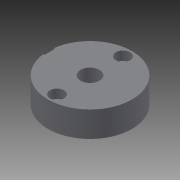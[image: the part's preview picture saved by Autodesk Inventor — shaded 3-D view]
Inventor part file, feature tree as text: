
AUTODESK INVENTOR PART (.ipt)
format: ipt  version: 2014 (Build 180170000, 170)  size: 225,792 bytes
history: native  units: in
note: dims shown in document units (in); Inventor stores cm internally (conversion verified against a paired STEP export)
features: other x189, sketch x10, hole x7, revolve x3, thread x1
ambient origin geometry x8: Origin, YZ Plane, XZ Plane, XY Plane, X Axis, Y Axis, Z Axis, Center Point
bodies: Solid1 (feature_tree)
feature tree (210):
  revolve  "Revolution1"  Angle=360.0deg
  revolve  "Revolution2"  Angle=360.0deg
  thread  "Thread1"  [1 undecoded]
  hole  "Hole1"  [1 undecoded]
  revolve  "Revolution3"  [1 undecoded]
  hole  "Hole2"  [1 undecoded]
  hole  "Hole3"  [1 undecoded]
  hole  "Hole4"  [1 undecoded]
  hole  "Hole5"  [1 undecoded]
  hole  "Hole6"  [1 undecoded]
  hole  "Hole7"  [1 undecoded]
  other  "a1_XY"
  other  "a1_YZ"
  other  "a1_ZX"
  other  "a1_X"
  other  "a1_Y"
  other  "a1_Z"
  other  "a1_Center"
  other  "a2_XY"
  other  "a2_YZ"
  other  "a2_ZX"
  other  "a2_X"
  other  "a2_Y"
  other  "a2_Z"
  other  "a2_Center"
  other  "ar3_XY"
  other  "ar3_YZ"
  other  "ar3_ZX"
  other  "ar3_X"
  other  "ar3_Y"
  other  "ar3_Z"
  other  "ar3_Center"
  other  "ar4_XY"
  other  "ar4_YZ"
  other  "ar4_ZX"
  other  "ar4_X"
  other  "ar4_Y"
  other  "ar4_Z"
  other  "ar4_Center"
  other  "ar5_XY"
  other  "ar5_YZ"
  other  "ar5_ZX"
  other  "ar5_X"
  other  "ar5_Y"
  other  "ar5_Z"
  other  "ar5_Center"
  other  "ar6_XY"
  other  "ar6_YZ"
  other  "ar6_ZX"
  other  "ar6_X"
  other  "ar6_Y"
  other  "ar6_Z"
  other  "ar6_Center"
  other  "b1_XY"
  other  "b1_YZ"
  other  "b1_ZX"
  other  "b1_X"
  other  "b1_Y"
  other  "b1_Z"
  other  "b1_Center"
  other  "c1_XY"
  other  "c1_YZ"
  other  "c1_ZX"
  other  "c1_X"
  other  "c1_Y"
  other  "c1_Z"
  other  "c1_Center"
  other  "c2_XY"
  other  "c2_YZ"
  other  "c2_ZX"
  other  "c2_X"
  other  "c2_Y"
  other  "c2_Z"
  other  "c2_Center"
  other  "d1_XY"
  other  "d1_YZ"
  other  "d1_ZX"
  other  "d1_X"
  other  "d1_Y"
  other  "d1_Z"
  other  "d1_Center"
  other  "d2_XY"
  other  "d2_YZ"
  other  "d2_ZX"
  other  "d2_X"
  other  "d2_Y"
  other  "d2_Z"
  other  "d2_Center"
  other  "j_XY"
  other  "j_YZ"
  other  "j_ZX"
  other  "j_X"
  other  "j_Y"
  other  "j_Z"
  other  "j_Center"
  other  "k1_XY"
  other  "k1_YZ"
  other  "k1_ZX"
  other  "k1_X"
  other  "k1_Y"
  other  "k1_Z"
  other  "k1_Center"
  other  "k2_XY"
  other  "k2_YZ"
  other  "k2_ZX"
  other  "k2_X"
  other  "k2_Y"
  other  "k2_Z"
  other  "k2_Center"
  other  "l1_XY"
  other  "l1_YZ"
  other  "l1_ZX"
  other  "l1_X"
  other  "l1_Y"
  other  "l1_Z"
  other  "l1_Center"
  other  "l2_XY"
  other  "l2_YZ"
  other  "l2_ZX"
  other  "l2_X"
  other  "l2_Y"
  other  "l2_Z"
  other  "l2_Center"
  other  "rg_XY"
  other  "rg_YZ"
  other  "rg_ZX"
  other  "rg_X"
  other  "rg_Y"
  other  "rg_Z"
  other  "rg_Center"
  other  "rh_XY"
  other  "rh_YZ"
  other  "rh_ZX"
  other  "rh_X"
  other  "rh_Y"
  other  "rh_Z"
  other  "rh_Center"
  other  "to_dummy_XY"
  other  "to_dummy_YZ"
  other  "to_dummy_ZX"
  other  "to_dummy_X"
  other  "to_dummy_Y"
  other  "to_dummy_Z"
  other  "to_dummy_Center"
  other  "to_nut_XY"
  other  "to_nut_YZ"
  other  "to_nut_ZX"
  other  "to_nut_X"
  other  "to_nut_Y"
  other  "to_nut_Z"
  other  "to_nut_Center"
  other  "to_rod_XY"
  other  "to_rod_YZ"
  other  "to_rod_ZX"
  other  "to_rod_X"
  other  "to_rod_Y"
  other  "to_rod_Z"
  other  "to_rod_Center"
  other  "to_tube_XY"
  other  "to_tube_YZ"
  other  "to_tube_ZX"
  other  "to_tube_X"
  other  "to_tube_Y"
  other  "to_tube_Z"
  other  "to_tube_Center"
  other  "to_wiper_XY"
  other  "to_wiper_YZ"
  other  "to_wiper_ZX"
  other  "to_wiper_X"
  other  "to_wiper_Y"
  other  "to_wiper_Z"
  other  "to_wiper_Center"
  other  "track1_XY"
  other  "track1_YZ"
  other  "track1_ZX"
  other  "track1_X"
  other  "track1_Y"
  other  "track1_Z"
  other  "track1_Center"
  other  "track2_XY"
  other  "track2_YZ"
  other  "track2_ZX"
  other  "track2_X"
  other  "track2_Y"
  other  "track2_Z"
  other  "track2_Center"
  other  "track3_XY"
  other  "track3_YZ"
  other  "track3_ZX"
  other  "track3_X"
  other  "track3_Y"
  other  "track3_Z"
  other  "track3_Center"
  other  "track4_XY"
  other  "track4_YZ"
  other  "track4_ZX"
  other  "track4_X"
  other  "track4_Y"
  other  "track4_Z"
  other  "track4_Center"
  sketch  "Sketch_1"  dims[d0=360.0deg d1=360.0deg]
  sketch  "Sketch_37"
  sketch  "Sketch3"  dims[d2=0.2in d3=0.06in]
  sketch  "Sketch_9"  dims[d33=0.12in d34=0.75in d35=0.375in d36=0.25in d37=0.5635in d38=0.1in d39=0.0in]
  sketch  "Sketch5"  dims[d4=0.252in d5=0.75in d6=0.375in d7=0.25in d8=0.5635in d9=0.34in d10=0.0in d11=360.0deg]
  sketch  "Sketch6"  dims[d12=0.12in d13=0.75in d14=0.188in d15=0.12in d16=0.5635in d17=0.34in d18=0.0in]
  sketch  "Sketch7"  dims[d19=0.12in d20=0.75in d21=0.188in d22=0.12in d23=0.5635in d24=0.34in d25=0.0in]
  sketch  "Sketch8"  dims[d26=0.12in d27=0.75in d28=0.375in d29=0.25in d30=0.5635in d31=0.1in d32=0.0in]
  sketch  "Sketch9"  dims[d40=0.12in d41=0.75in d42=0.375in d43=0.25in d44=0.5635in d45=0.1in d46=0.0in]
  sketch  "Sketch10"  dims[d47=0.12in d48=0.75in d49=0.375in d50=0.25in d51=0.5635in d52=0.1in d53=0.0in]
note: 9 required parameter values undecoded (feature->parameter linkage not recoverable at this tier; creation-order binding heuristic only, values carry confidence <= 0.55)
